# Revit family: Valve_Trim-DXV-Equility-D35109600_Series
name_source: partatom
category: Plumbing Fixtures
units: mm (PartAtom-declared; Revit-internal decimal feet)

## family parameters
Cut with Voids When Loaded = No
Host = Face
OmniClass Number = 23.45.05.14.21.11
OmniClass Title = Bath/Shower Units
Part Type = Normal
Room Calculation Point = No
Round Connector Dimension = Use Radius
Shared = Yes

## types (6) — shared parameters
Assembly Code = D2010710
CW Connection = No
CWFU = 3
Default Elevation = 40"
HW Connection = No
HWFU = 3
Height = 8 3/8"
Installation Instruction Link = https://dxv01.blob.core.windows.net
Installation Type = Wall Mounted
Length = 3 3/16"
Manufacturer = DXV
Price = Prices may vary. Please consult Manufacturer Representative for most up-to-date price list.
Product Documentation Link = https://dxv01.blob.core.windows.net
Product Page URL = https://www.dxv.com
Revised Date = 07/28/2021
Shower Rough Location = 1 5/8"
Tempered Water Connection = No
URL = http://www.dxv.com
Vent Connection = No
WFU = 4
Warranty Documentation Link = https://www.dxv.com
Waste Connection = No
Width = 6 11/16"

## per-type parameters (varying)
| type | Description | Finish | Material | Red and Blue Indicator Marking |
| D35109600.100 | Equility Pressure Balance Tub/Shower Valve Trim | Brass-DXV-100-Polished Chrome | Brass-DXV-100-Polished Chrome | No |
| D35109600.144 | Equility Pressure Balance Tub/Shower Valve Trim | Brass-DXV-144-Brushed Nickel | Brass-DXV-144-Brushed Nickel | No |
| D35109600.243 | Equility Pressure Balance Tub/Shower Valve Trim | Brass-DXV-243-Matte Black | Brass-DXV-243-Matte Black | No |
| D35109600RB.100 | Equility Pressure Balance Tub/Shower Valve Trim With Diverter | Brass-DXV-100-Polished Chrome | Brass-DXV-100-Polished Chrome | Yes |
| D35109600RB.144 | Equility Pressure Balance Tub/Shower Valve Trim With Diverter | Brass-DXV-144-Brushed Nickel | Brass-DXV-144-Brushed Nickel | Yes |
| D35109600RB.243 | Equility Pressure Balance Tub/Shower Valve Trim With Diverter | Brass-DXV-243-Matte Black | Brass-DXV-243-Matte Black | Yes |

note: column(s) folded — value = type name in every type: Model

## geometry (parser evidence)
native form markers: Sweep x3
no freeform markers — native parametric forms only
